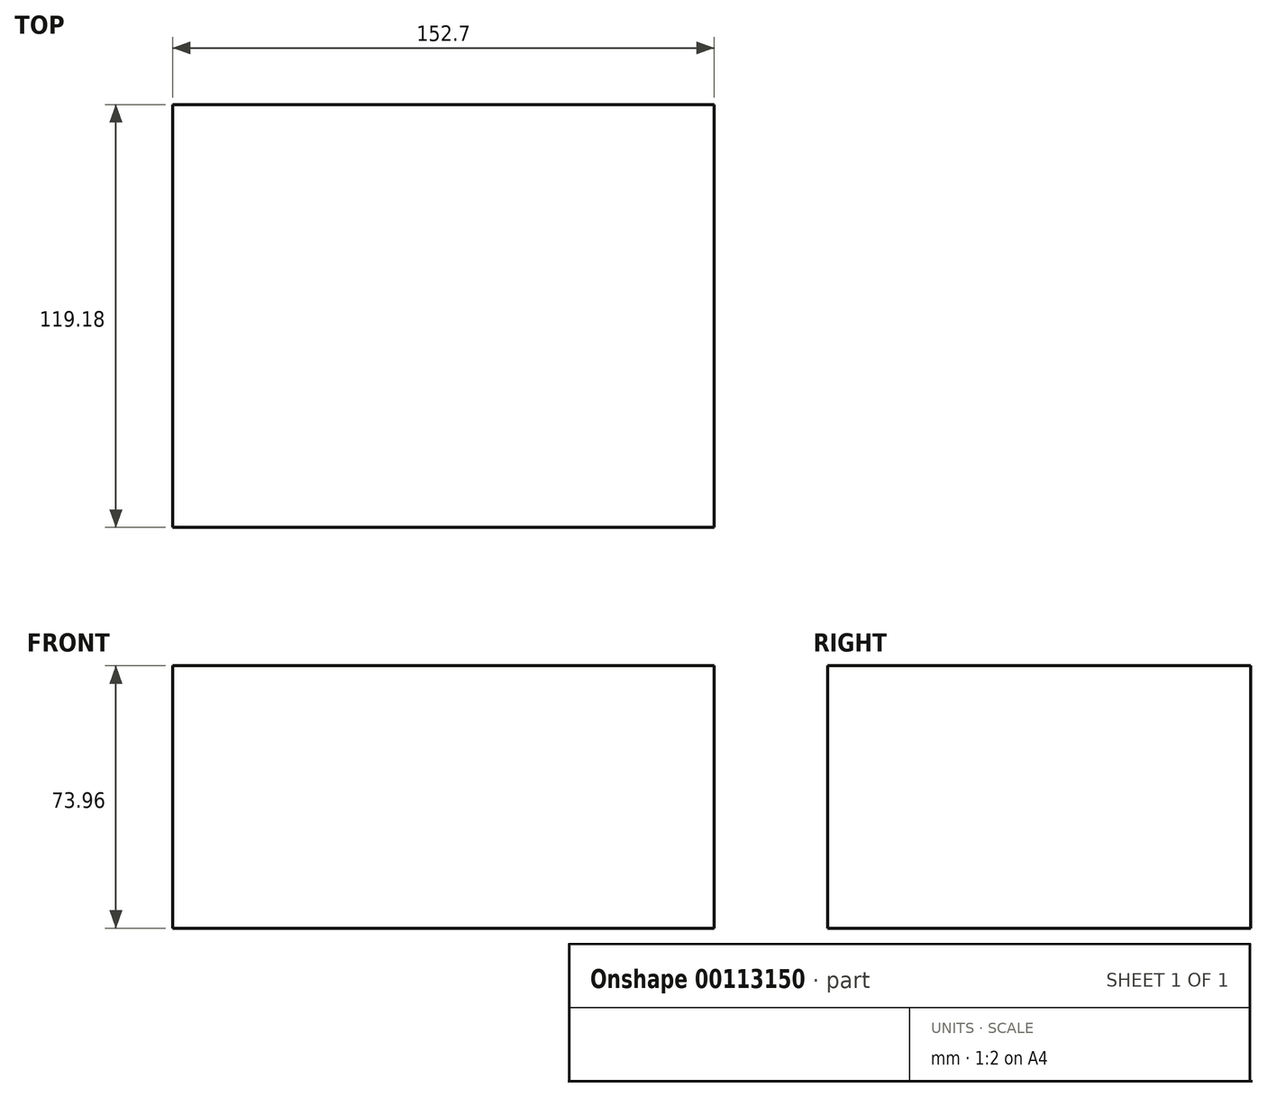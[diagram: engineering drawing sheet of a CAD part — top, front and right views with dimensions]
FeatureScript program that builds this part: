
annotation { "Feature Type Name" : "Feature", "Feature Type Description" : "" }
export const myFeature = defineFeature(function(context is Context, id is Id, definition is map)
    precondition{}
    {
        {
            var Q0;
            Q0=qCreatedBy(makeId("Top.planeOp"),FACE);
            var sketch = newSketch(context, id + "F0", { "sketchPlane" : qUnion([Q0])});
            skLineSegment(sketch, "E0.bottom", {"start": v(-112.88, -58.07) * mm, "end": v(39.82, -58.07) * mm});
            skLineSegment(sketch, "E0.top", {"start": v(-112.88, 61.1) * mm, "end": v(39.82, 61.1) * mm});
            skLineSegment(sketch, "E0.left", {"start": v(-112.88, -58.07) * mm, "end": v(-112.88, 61.1) * mm});
            skLineSegment(sketch, "E0.right", {"start": v(39.82, -58.07) * mm, "end": v(39.82, 61.1) * mm});
            skLineSegment(sketch, "E1.bottom", {"start": v(-102.47, 61.1) * mm, "end": v(30.88, 61.1) * mm});
            skLineSegment(sketch, "E1.top", {"start": v(-102.47, -58.07) * mm, "end": v(30.88, -58.07) * mm});
            skLineSegment(sketch, "E1.left", {"start": v(-102.47, 61.1) * mm, "end": v(-102.47, -58.07) * mm});
            skLineSegment(sketch, "E1.right", {"start": v(30.88, 61.1) * mm, "end": v(30.88, -58.07) * mm});
            skSolve(sketch);
        }
        {
            var Q0;
            Q0 = qSketchRegion(id + "F0", true);
            extrude(context, id + "F1", {"entities" : qUnion([Q0]), "depth" : 73.96 * mm});
        }
    });
